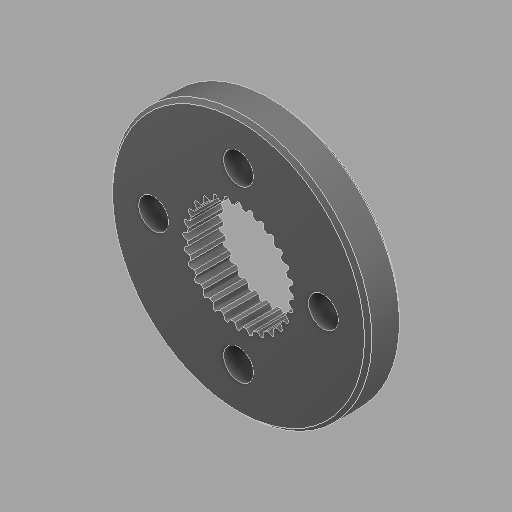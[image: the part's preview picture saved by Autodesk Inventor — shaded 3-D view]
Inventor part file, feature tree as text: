
AUTODESK INVENTOR PART (.ipt)
format: ipt  version: 2024.2 (Build 282272000, 272)  size: 256,512 bytes
history: native  units: in
note: dims shown in document units (in); Inventor stores cm internally (conversion verified against a paired STEP export)
features: chamfer x1
ambient origin geometry x8: Origin, YZ Plane, XZ Plane, XY Plane, X Axis, Y Axis, Z Axis, Center Point
bodies: Solid1 (feature_tree)
feature tree (1):
  chamfer  "Chamfer1"  [1 undecoded]
note: 1 required parameter value undecoded (feature->parameter linkage not recoverable at this tier; creation-order binding heuristic only, values carry confidence <= 0.55)
